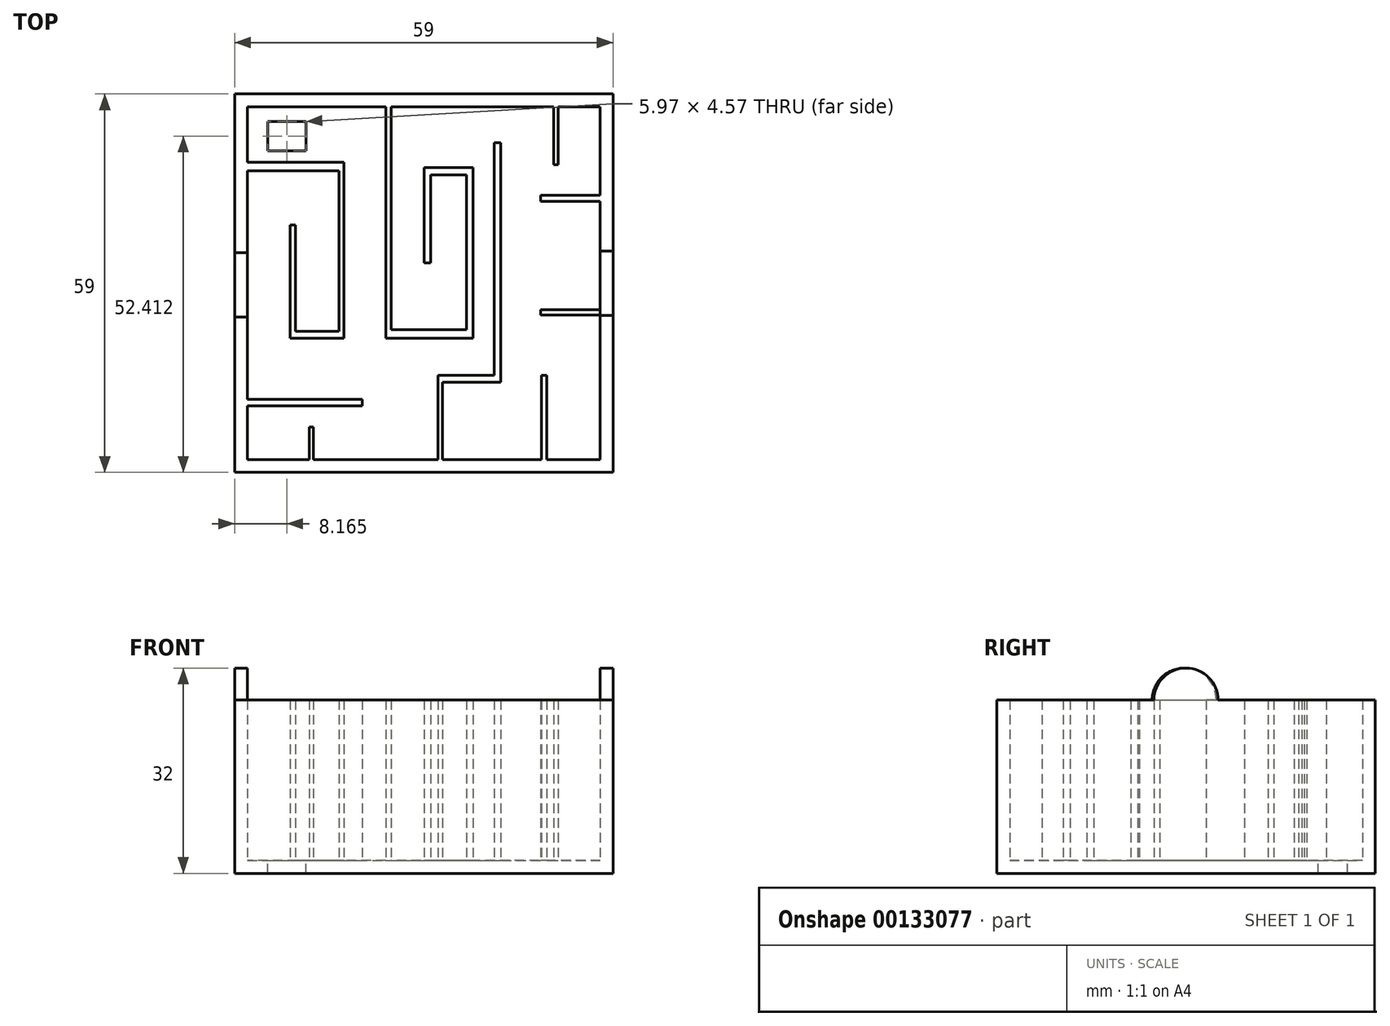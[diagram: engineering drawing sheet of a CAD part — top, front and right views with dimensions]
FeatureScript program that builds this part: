
annotation { "Feature Type Name" : "Feature", "Feature Type Description" : "" }
export const myFeature = defineFeature(function(context is Context, id is Id, definition is map)
    precondition{}
    {
        {
            var Q0;
            Q0=qCreatedBy(makeId("Top.planeOp"),FACE);
            var sketch = newSketch(context, id + "F0", { "sketchPlane" : qUnion([Q0])});
            skLineSegment(sketch, "E0.bottom", {"start": v(0, 0) * mm, "end": v(55, 0) * mm});
            skLineSegment(sketch, "E0.top", {"start": v(0, 55) * mm, "end": v(55, 55) * mm});
            skLineSegment(sketch, "E0.left", {"start": v(0, 0) * mm, "end": v(0, 55) * mm});
            skLineSegment(sketch, "E0.right", {"start": v(55, 0) * mm, "end": v(55, 55) * mm});
            skSolve(sketch);
        }
        {
            var Q0;
            Q0=makeQuery(id+"F0.imprint","IMPRINT",FACE,{"disambiguationData":[TD([[makeQuery(id+"F0.imprint","IMPRINT",EDGE,{"derivedFrom":sQuery(id+"F0.wireOp",EDGE,"E0.bottom")}),1.0]])]});
            extrude(context, id + "F1", {"entities" : qUnion([Q0]), "depth" : 2 * mm});
        }
        {
            var Q0;
            Q0=makeQuery(id+"F1.opExtrude","CAP_FACE",FACE,{"disambiguationData":[OSD([sQuery(id+"F0.wireOp",EDGE,"E0.bottom"),sQuery(id+"F0.wireOp",EDGE,"E0.top"),sQuery(id+"F0.wireOp",EDGE,"E0.left"),sQuery(id+"F0.wireOp",EDGE,"E0.right")])],"isStart":false});
            var sketch = newSketch(context, id + "F2", { "sketchPlane" : qUnion([Q0])});
            skLineSegment(sketch, "E1.bottom", {"start": v(46.66, 0) * mm, "end": v(45.82, 0) * mm});
            skLineSegment(sketch, "E1.top", {"start": v(46.66, 13.1) * mm, "end": v(45.82, 13.1) * mm});
            skLineSegment(sketch, "E1.left", {"start": v(46.66, 0) * mm, "end": v(46.66, 13.1) * mm});
            skLineSegment(sketch, "E1.right", {"start": v(45.82, 0) * mm, "end": v(45.82, 13.1) * mm});
            skLineSegment(sketch, "E2.bottom", {"start": v(0, 46.34) * mm, "end": v(14.3, 46.34) * mm});
            skLineSegment(sketch, "E2.top", {"start": v(0, 45.02) * mm, "end": v(14.3, 45.02) * mm});
            skLineSegment(sketch, "E2.left", {"start": v(0, 46.34) * mm, "end": v(0, 45.02) * mm});
            skLineSegment(sketch, "E2.right", {"start": v(14.3, 46.34) * mm, "end": v(14.3, 45.02) * mm});
            skLineSegment(sketch, "E3.bottom", {"start": v(14.3, 46.34) * mm, "end": v(15.04, 46.34) * mm});
            skLineSegment(sketch, "E3.top", {"start": v(14.3, 19.96) * mm, "end": v(15.04, 19.96) * mm});
            skLineSegment(sketch, "E3.left", {"start": v(14.3, 46.34) * mm, "end": v(14.3, 19.96) * mm});
            skLineSegment(sketch, "E3.right", {"start": v(15.04, 46.34) * mm, "end": v(15.04, 19.96) * mm});
            skLineSegment(sketch, "E4.bottom", {"start": v(15.04, 19.96) * mm, "end": v(7.49, 19.96) * mm});
            skLineSegment(sketch, "E4.top", {"start": v(15.04, 18.9) * mm, "end": v(7.49, 18.9) * mm});
            skLineSegment(sketch, "E4.left", {"start": v(15.04, 19.96) * mm, "end": v(15.04, 18.9) * mm});
            skLineSegment(sketch, "E4.right", {"start": v(7.49, 19.96) * mm, "end": v(7.49, 18.9) * mm});
            skLineSegment(sketch, "E5.bottom", {"start": v(7.49, 18.9) * mm, "end": v(6.65, 18.9) * mm});
            skLineSegment(sketch, "E5.top", {"start": v(7.49, 36.58) * mm, "end": v(6.65, 36.58) * mm});
            skLineSegment(sketch, "E5.left", {"start": v(7.49, 18.9) * mm, "end": v(7.49, 36.58) * mm});
            skLineSegment(sketch, "E5.right", {"start": v(6.65, 18.9) * mm, "end": v(6.65, 36.58) * mm});
            skLineSegment(sketch, "E6.bottom", {"start": v(0, 9.41) * mm, "end": v(17.94, 9.41) * mm});
            skLineSegment(sketch, "E6.top", {"start": v(0, 8.36) * mm, "end": v(17.94, 8.36) * mm});
            skLineSegment(sketch, "E6.left", {"start": v(0, 9.41) * mm, "end": v(0, 8.36) * mm});
            skLineSegment(sketch, "E6.right", {"start": v(17.94, 9.41) * mm, "end": v(17.94, 8.36) * mm});
            skLineSegment(sketch, "E7.bottom", {"start": v(10.29, 0) * mm, "end": v(9.63, 0) * mm});
            skLineSegment(sketch, "E7.top", {"start": v(10.29, 5.06) * mm, "end": v(9.63, 5.06) * mm});
            skLineSegment(sketch, "E7.left", {"start": v(10.29, 0) * mm, "end": v(10.29, 5.06) * mm});
            skLineSegment(sketch, "E7.right", {"start": v(9.63, 0) * mm, "end": v(9.63, 5.06) * mm});
            skLineSegment(sketch, "E8.bottom", {"start": v(21.57, 55) * mm, "end": v(22.41, 55) * mm});
            skLineSegment(sketch, "E8.top", {"start": v(21.57, 18.9) * mm, "end": v(22.41, 18.9) * mm});
            skLineSegment(sketch, "E8.left", {"start": v(21.57, 55) * mm, "end": v(21.57, 18.9) * mm});
            skLineSegment(sketch, "E8.right", {"start": v(22.41, 55) * mm, "end": v(22.41, 18.9) * mm});
            skLineSegment(sketch, "E9.bottom", {"start": v(22.41, 18.9) * mm, "end": v(35.19, 18.9) * mm});
            skLineSegment(sketch, "E9.top", {"start": v(22.41, 20.23) * mm, "end": v(35.19, 20.23) * mm});
            skLineSegment(sketch, "E9.left", {"start": v(22.41, 18.9) * mm, "end": v(22.41, 20.23) * mm});
            skLineSegment(sketch, "E9.right", {"start": v(35.19, 18.9) * mm, "end": v(35.19, 20.23) * mm});
            skLineSegment(sketch, "E10.bottom", {"start": v(35.19, 20.23) * mm, "end": v(34.16, 20.23) * mm});
            skLineSegment(sketch, "E10.top", {"start": v(35.19, 44.36) * mm, "end": v(34.16, 44.36) * mm});
            skLineSegment(sketch, "E10.left", {"start": v(35.19, 20.23) * mm, "end": v(35.19, 44.36) * mm});
            skLineSegment(sketch, "E10.right", {"start": v(34.16, 20.23) * mm, "end": v(34.16, 44.36) * mm});
            skLineSegment(sketch, "E11.bottom", {"start": v(35.19, 44.36) * mm, "end": v(28.57, 44.36) * mm});
            skLineSegment(sketch, "E11.top", {"start": v(35.19, 45.55) * mm, "end": v(28.57, 45.55) * mm});
            skLineSegment(sketch, "E11.left", {"start": v(35.19, 44.36) * mm, "end": v(35.19, 45.55) * mm});
            skLineSegment(sketch, "E11.right", {"start": v(28.57, 44.36) * mm, "end": v(28.57, 45.55) * mm});
            skLineSegment(sketch, "E12.bottom", {"start": v(28.57, 45.55) * mm, "end": v(27.54, 45.55) * mm});
            skLineSegment(sketch, "E12.top", {"start": v(28.57, 30.65) * mm, "end": v(27.54, 30.65) * mm});
            skLineSegment(sketch, "E12.left", {"start": v(28.57, 45.55) * mm, "end": v(28.57, 30.65) * mm});
            skLineSegment(sketch, "E12.right", {"start": v(27.54, 45.55) * mm, "end": v(27.54, 30.65) * mm});
            skLineSegment(sketch, "E13.left", {"start": v(55, 27.5) * mm, "end": v(55, 26.03) * mm});
            skLineSegment(sketch, "E14.bottom", {"start": v(29.69, 0) * mm, "end": v(30.43, 0) * mm});
            skLineSegment(sketch, "E14.top", {"start": v(29.69, 13.1) * mm, "end": v(30.43, 13.1) * mm});
            skLineSegment(sketch, "E14.left", {"start": v(29.69, 0) * mm, "end": v(29.69, 13.1) * mm});
            skLineSegment(sketch, "E14.right", {"start": v(30.43, 0) * mm, "end": v(30.43, 13.1) * mm});
            skLineSegment(sketch, "E15.bottom", {"start": v(29.69, 13.1) * mm, "end": v(38.45, 13.1) * mm});
            skLineSegment(sketch, "E15.top", {"start": v(29.69, 12.05) * mm, "end": v(38.45, 12.05) * mm});
            skLineSegment(sketch, "E15.left", {"start": v(29.69, 13.1) * mm, "end": v(29.69, 12.05) * mm});
            skLineSegment(sketch, "E15.right", {"start": v(38.45, 13.1) * mm, "end": v(38.45, 12.05) * mm});
            skLineSegment(sketch, "E16.bottom", {"start": v(38.45, 12.05) * mm, "end": v(39.48, 12.05) * mm});
            skLineSegment(sketch, "E16.top", {"start": v(38.45, 49.38) * mm, "end": v(39.48, 49.38) * mm});
            skLineSegment(sketch, "E16.left", {"start": v(38.45, 12.05) * mm, "end": v(38.45, 49.38) * mm});
            skLineSegment(sketch, "E16.right", {"start": v(39.48, 12.05) * mm, "end": v(39.48, 49.38) * mm});
            skLineSegment(sketch, "E17.bottom", {"start": v(55, 41.2) * mm, "end": v(45.73, 41.2) * mm});
            skLineSegment(sketch, "E17.top", {"start": v(55, 40.28) * mm, "end": v(45.73, 40.28) * mm});
            skLineSegment(sketch, "E17.left", {"start": v(55, 41.2) * mm, "end": v(55, 40.28) * mm});
            skLineSegment(sketch, "E17.right", {"start": v(45.73, 41.2) * mm, "end": v(45.73, 40.28) * mm});
            skLineSegment(sketch, "E18.bottom", {"start": v(47.78, 55) * mm, "end": v(48.43, 55) * mm});
            skLineSegment(sketch, "E18.top", {"start": v(47.78, 45.95) * mm, "end": v(48.43, 45.95) * mm});
            skLineSegment(sketch, "E18.left", {"start": v(47.78, 55) * mm, "end": v(47.78, 45.95) * mm});
            skLineSegment(sketch, "E18.right", {"start": v(48.43, 55) * mm, "end": v(48.43, 45.95) * mm});
            skLineSegment(sketch, "E19.bottom", {"start": v(55, 23.38) * mm, "end": v(45.7, 23.38) * mm});
            skLineSegment(sketch, "E19.top", {"start": v(55, 22.5) * mm, "end": v(45.7, 22.5) * mm});
            skLineSegment(sketch, "E19.left", {"start": v(55, 23.38) * mm, "end": v(55, 22.5) * mm});
            skLineSegment(sketch, "E19.right", {"start": v(45.7, 23.38) * mm, "end": v(45.7, 22.5) * mm});
            skSolve(sketch);
        }
        {
            var Q0;
            Q0 = qSketchRegion(id + "F2", true);
            extrude(context, id + "F3", {"entities" : qUnion([Q0]), "operationType" : NewBodyOperationType.ADD, "depth" : 25 * mm});
        }
        {
            var Q0;
            Q0=makeQuery(id+"F3.boolean.opBoolean","MERGE",FACE,{"derivedFrom":[makeQuery(id+"F1.opExtrude","SWEPT_FACE",FACE,{"disambiguationData":[OSD([sQuery(id+"F0.wireOp",EDGE,"E0.bottom")])]}),makeQuery(id+"F3.opExtrude","SWEPT_FACE",FACE,{"disambiguationData":[OSD([sQuery(id+"F2.wireOp",EDGE,"E1.bottom")])]}),makeQuery(id+"F3.opExtrude","SWEPT_FACE",FACE,{"disambiguationData":[OSD([sQuery(id+"F2.wireOp",EDGE,"E7.bottom")])]}),makeQuery(id+"F3.opExtrude","SWEPT_FACE",FACE,{"disambiguationData":[OSD([sQuery(id+"F2.wireOp",EDGE,"E14.bottom")])]})]});
            var sketch = newSketch(context, id + "F4", { "sketchPlane" : qUnion([Q0])});
            skLineSegment(sketch, "E20.bottom", {"start": v(0, 2) * mm, "end": v(55, 2) * mm});
            skLineSegment(sketch, "E20.top", {"start": v(0, 0) * mm, "end": v(55, 0) * mm});
            skLineSegment(sketch, "E20.left", {"start": v(0, 2) * mm, "end": v(0, 0) * mm});
            skLineSegment(sketch, "E20.right", {"start": v(55, 2) * mm, "end": v(55, 0) * mm});
            skSolve(sketch);
        }
        {
            var Q0;
            Q0=makeQuery(id+"F4.imprint","IMPRINT",FACE,{"disambiguationData":[TD([[makeQuery(id+"F4.imprint","IMPRINT",EDGE,{"derivedFrom":sQuery(id+"F4.wireOp",EDGE,"E20.top")}),1.0]])]});
            extrude(context, id + "F5", {"entities" : qUnion([Q0]), "operationType" : NewBodyOperationType.ADD, "depth" : 2 * mm});
        }
        {
            var Q0;
            Q0=makeQuery(id+"F5.boolean.opBoolean","MERGE",FACE,{"derivedFrom":[makeQuery(id+"F1.opExtrude","CAP_FACE",FACE,{"disambiguationData":[OSD([sQuery(id+"F0.wireOp",EDGE,"E0.bottom"),sQuery(id+"F0.wireOp",EDGE,"E0.top"),sQuery(id+"F0.wireOp",EDGE,"E0.left"),sQuery(id+"F0.wireOp",EDGE,"E0.right")])],"isStart":false}),makeQuery(id+"F5.opExtrude","SWEPT_FACE",FACE,{"disambiguationData":[OSD([sQuery(id+"F4.wireOp",EDGE,"E20.bottom")])]})]});
            var sketch = newSketch(context, id + "F6", { "sketchPlane" : qUnion([Q0])});
            skLineSegment(sketch, "E21.bottom", {"start": v(0, 0) * mm, "end": v(55, 0) * mm});
            skLineSegment(sketch, "E21.top", {"start": v(0, -2) * mm, "end": v(55, -2) * mm});
            skLineSegment(sketch, "E21.left", {"start": v(0, 0) * mm, "end": v(0, -2) * mm});
            skLineSegment(sketch, "E21.right", {"start": v(55, 0) * mm, "end": v(55, -2) * mm});
            skSolve(sketch);
        }
        {
            var Q0;
            Q0=makeQuery(id+"F6.imprint","IMPRINT",FACE,{"disambiguationData":[TD([[makeQuery(id+"F6.imprint","IMPRINT",EDGE,{"derivedFrom":sQuery(id+"F6.wireOp",EDGE,"E21.top")}),1.0]])]});
            extrude(context, id + "F7", {"entities" : qUnion([Q0]), "operationType" : NewBodyOperationType.ADD, "depth" : 25 * mm});
        }
        {
            var Q0;
            Q0=makeQuery(id+"F7.boolean.opBoolean","MERGE",FACE,{"derivedFrom":[makeQuery(id+"F5.boolean.opBoolean","MERGE",FACE,{"derivedFrom":[makeQuery(id+"F3.boolean.opBoolean","MERGE",FACE,{"derivedFrom":[makeQuery(id+"F1.opExtrude","SWEPT_FACE",FACE,{"disambiguationData":[OSD([sQuery(id+"F0.wireOp",EDGE,"E0.left")])]}),makeQuery(id+"F3.opExtrude","SWEPT_FACE",FACE,{"disambiguationData":[OSD([sQuery(id+"F2.wireOp",EDGE,"E2.left")])]}),makeQuery(id+"F3.opExtrude","SWEPT_FACE",FACE,{"disambiguationData":[OSD([sQuery(id+"F2.wireOp",EDGE,"E6.left")])]})]}),makeQuery(id+"F5.opExtrude","SWEPT_FACE",FACE,{"disambiguationData":[OSD([sQuery(id+"F4.wireOp",EDGE,"E20.left")])]})]}),makeQuery(id+"F7.opExtrude","SWEPT_FACE",FACE,{"disambiguationData":[OSD([sQuery(id+"F6.wireOp",EDGE,"E21.left")])]})]});
            var sketch = newSketch(context, id + "F8", { "sketchPlane" : qUnion([Q0])});
            skLineSegment(sketch, "E22.bottom", {"start": v(-55, 2) * mm, "end": v(2, 2) * mm});
            skLineSegment(sketch, "E22.top", {"start": v(-55, 0) * mm, "end": v(2, 0) * mm});
            skLineSegment(sketch, "E22.left", {"start": v(-55, 2) * mm, "end": v(-55, 0) * mm});
            skLineSegment(sketch, "E22.right", {"start": v(2, 2) * mm, "end": v(2, 0) * mm});
            skSolve(sketch);
        }
        {
            var Q0;
            Q0 = qSketchRegion(id + "F8", true);
            extrude(context, id + "F9", {"entities" : qUnion([Q0]), "operationType" : NewBodyOperationType.ADD, "depth" : 2 * mm});
        }
        {
            var Q0;
            Q0=makeQuery(id+"F9.boolean.opBoolean","MERGE",FACE,{"derivedFrom":[makeQuery(id+"F5.boolean.opBoolean","MERGE",FACE,{"derivedFrom":[makeQuery(id+"F1.opExtrude","CAP_FACE",FACE,{"disambiguationData":[OSD([sQuery(id+"F0.wireOp",EDGE,"E0.bottom"),sQuery(id+"F0.wireOp",EDGE,"E0.top"),sQuery(id+"F0.wireOp",EDGE,"E0.left"),sQuery(id+"F0.wireOp",EDGE,"E0.right")])],"isStart":false}),makeQuery(id+"F5.opExtrude","SWEPT_FACE",FACE,{"disambiguationData":[OSD([sQuery(id+"F4.wireOp",EDGE,"E20.bottom")])]})]}),makeQuery(id+"F9.opExtrude","SWEPT_FACE",FACE,{"disambiguationData":[OSD([sQuery(id+"F8.wireOp",EDGE,"E22.bottom")])]})]});
            var sketch = newSketch(context, id + "F10", { "sketchPlane" : qUnion([Q0])});
            skLineSegment(sketch, "E23.bottom", {"start": v(0, 55) * mm, "end": v(-2, 55) * mm});
            skLineSegment(sketch, "E23.top", {"start": v(0, -2) * mm, "end": v(-2, -2) * mm});
            skLineSegment(sketch, "E23.left", {"start": v(0, 55) * mm, "end": v(0, -2) * mm});
            skLineSegment(sketch, "E23.right", {"start": v(-2, 55) * mm, "end": v(-2, -2) * mm});
            skSolve(sketch);
        }
        {
            var Q0;
            Q0 = qSketchRegion(id + "F10", true);
            extrude(context, id + "F11", {"entities" : qUnion([Q0]), "operationType" : NewBodyOperationType.ADD, "depth" : 25 * mm});
        }
        {
            var Q0;
            Q0=makeQuery(id+"F11.boolean.opBoolean","MERGE",FACE,{"derivedFrom":[makeQuery(id+"F9.boolean.opBoolean","MERGE",FACE,{"derivedFrom":[makeQuery(id+"F3.boolean.opBoolean","MERGE",FACE,{"derivedFrom":[makeQuery(id+"F1.opExtrude","SWEPT_FACE",FACE,{"disambiguationData":[OSD([sQuery(id+"F0.wireOp",EDGE,"E0.top")])]}),makeQuery(id+"F3.opExtrude","SWEPT_FACE",FACE,{"disambiguationData":[OSD([sQuery(id+"F2.wireOp",EDGE,"E8.bottom")])]}),makeQuery(id+"F3.opExtrude","SWEPT_FACE",FACE,{"disambiguationData":[OSD([sQuery(id+"F2.wireOp",EDGE,"E18.bottom")])]})]}),makeQuery(id+"F9.opExtrude","SWEPT_FACE",FACE,{"disambiguationData":[OSD([sQuery(id+"F8.wireOp",EDGE,"E22.left")])]})]}),makeQuery(id+"F11.opExtrude","SWEPT_FACE",FACE,{"disambiguationData":[OSD([sQuery(id+"F10.wireOp",EDGE,"E23.bottom")])]})]});
            var sketch = newSketch(context, id + "F12", { "sketchPlane" : qUnion([Q0])});
            skLineSegment(sketch, "E24.bottom", {"start": v(2, 0) * mm, "end": v(-55, 0) * mm});
            skLineSegment(sketch, "E24.top", {"start": v(2, 2) * mm, "end": v(-55, 2) * mm});
            skLineSegment(sketch, "E24.left", {"start": v(2, 0) * mm, "end": v(2, 2) * mm});
            skLineSegment(sketch, "E24.right", {"start": v(-55, 0) * mm, "end": v(-55, 2) * mm});
            skSolve(sketch);
        }
        {
            var Q0;
            Q0=makeQuery(id+"F12.imprint","IMPRINT",FACE,{"disambiguationData":[TD([[makeQuery(id+"F12.imprint","IMPRINT",EDGE,{"derivedFrom":sQuery(id+"F12.wireOp",EDGE,"E24.bottom")}),-1.0]])]});
            extrude(context, id + "F13", {"entities" : qUnion([Q0]), "operationType" : NewBodyOperationType.ADD, "depth" : 2 * mm});
        }
        {
            var Q0;
            Q0=makeQuery(id+"F13.boolean.opBoolean","MERGE",FACE,{"derivedFrom":[makeQuery(id+"F9.boolean.opBoolean","MERGE",FACE,{"derivedFrom":[makeQuery(id+"F5.boolean.opBoolean","MERGE",FACE,{"derivedFrom":[makeQuery(id+"F1.opExtrude","CAP_FACE",FACE,{"disambiguationData":[OSD([sQuery(id+"F0.wireOp",EDGE,"E0.bottom"),sQuery(id+"F0.wireOp",EDGE,"E0.top"),sQuery(id+"F0.wireOp",EDGE,"E0.left"),sQuery(id+"F0.wireOp",EDGE,"E0.right")])],"isStart":false}),makeQuery(id+"F5.opExtrude","SWEPT_FACE",FACE,{"disambiguationData":[OSD([sQuery(id+"F4.wireOp",EDGE,"E20.bottom")])]})]}),makeQuery(id+"F9.opExtrude","SWEPT_FACE",FACE,{"disambiguationData":[OSD([sQuery(id+"F8.wireOp",EDGE,"E22.bottom")])]})]}),makeQuery(id+"F13.opExtrude","SWEPT_FACE",FACE,{"disambiguationData":[OSD([sQuery(id+"F12.wireOp",EDGE,"E24.top")])]})]});
            var sketch = newSketch(context, id + "F14", { "sketchPlane" : qUnion([Q0])});
            skLineSegment(sketch, "E25.bottom", {"start": v(55, 57) * mm, "end": v(-2, 57) * mm});
            skLineSegment(sketch, "E25.top", {"start": v(55, 55) * mm, "end": v(-2, 55) * mm});
            skLineSegment(sketch, "E25.left", {"start": v(55, 57) * mm, "end": v(55, 55) * mm});
            skLineSegment(sketch, "E25.right", {"start": v(-2, 57) * mm, "end": v(-2, 55) * mm});
            skSolve(sketch);
        }
        {
            var Q0;
            Q0=makeQuery(id+"F14.imprint","IMPRINT",FACE,{"disambiguationData":[TD([[makeQuery(id+"F14.imprint","IMPRINT",EDGE,{"derivedFrom":sQuery(id+"F14.wireOp",EDGE,"E25.bottom")}),-1.0]])]});
            extrude(context, id + "F15", {"entities" : qUnion([Q0]), "operationType" : NewBodyOperationType.ADD, "depth" : 25 * mm});
        }
        {
            var Q0;
            Q0=makeQuery(id+"F15.boolean.opBoolean","MERGE",FACE,{"derivedFrom":[makeQuery(id+"F13.boolean.opBoolean","MERGE",FACE,{"derivedFrom":[makeQuery(id+"F7.boolean.opBoolean","MERGE",FACE,{"derivedFrom":[makeQuery(id+"F5.boolean.opBoolean","MERGE",FACE,{"derivedFrom":[makeQuery(id+"F3.boolean.opBoolean","MERGE",FACE,{"derivedFrom":[makeQuery(id+"F1.opExtrude","SWEPT_FACE",FACE,{"disambiguationData":[OSD([sQuery(id+"F0.wireOp",EDGE,"E0.right")])]}),makeQuery(id+"F3.opExtrude","SWEPT_FACE",FACE,{"disambiguationData":[OSD([sQuery(id+"F2.wireOp",EDGE,"E17.left")])]}),makeQuery(id+"F3.opExtrude","SWEPT_FACE",FACE,{"disambiguationData":[OSD([sQuery(id+"F2.wireOp",EDGE,"E19.left")])]})]}),makeQuery(id+"F5.opExtrude","SWEPT_FACE",FACE,{"disambiguationData":[OSD([sQuery(id+"F4.wireOp",EDGE,"E20.right")])]})]}),makeQuery(id+"F7.opExtrude","SWEPT_FACE",FACE,{"disambiguationData":[OSD([sQuery(id+"F6.wireOp",EDGE,"E21.right")])]})]}),makeQuery(id+"F13.opExtrude","SWEPT_FACE",FACE,{"disambiguationData":[OSD([sQuery(id+"F12.wireOp",EDGE,"E24.right")])]})]}),makeQuery(id+"F15.opExtrude","SWEPT_FACE",FACE,{"disambiguationData":[OSD([sQuery(id+"F14.wireOp",EDGE,"E25.left")])]})]});
            var sketch = newSketch(context, id + "F16", { "sketchPlane" : qUnion([Q0])});
            skLineSegment(sketch, "E26.bottom", {"start": v(-2, 0) * mm, "end": v(57, 0) * mm});
            skLineSegment(sketch, "E26.top", {"start": v(-2, 2) * mm, "end": v(57, 2) * mm});
            skLineSegment(sketch, "E26.left", {"start": v(-2, 0) * mm, "end": v(-2, 2) * mm});
            skLineSegment(sketch, "E26.right", {"start": v(57, 0) * mm, "end": v(57, 2) * mm});
            skSolve(sketch);
        }
        {
            var Q0;
            Q0=makeQuery(id+"F16.imprint","IMPRINT",FACE,{"disambiguationData":[TD([[makeQuery(id+"F16.imprint","IMPRINT",EDGE,{"derivedFrom":sQuery(id+"F16.wireOp",EDGE,"E26.bottom")}),1.0]])]});
            extrude(context, id + "F17", {"entities" : qUnion([Q0]), "operationType" : NewBodyOperationType.ADD, "depth" : 2 * mm});
        }
        {
            var Q0;
            Q0=makeQuery(id+"F17.boolean.opBoolean","MERGE",FACE,{"derivedFrom":[makeQuery(id+"F13.boolean.opBoolean","MERGE",FACE,{"derivedFrom":[makeQuery(id+"F9.boolean.opBoolean","MERGE",FACE,{"derivedFrom":[makeQuery(id+"F5.boolean.opBoolean","MERGE",FACE,{"derivedFrom":[makeQuery(id+"F1.opExtrude","CAP_FACE",FACE,{"disambiguationData":[OSD([sQuery(id+"F0.wireOp",EDGE,"E0.bottom"),sQuery(id+"F0.wireOp",EDGE,"E0.top"),sQuery(id+"F0.wireOp",EDGE,"E0.left"),sQuery(id+"F0.wireOp",EDGE,"E0.right")])],"isStart":false}),makeQuery(id+"F5.opExtrude","SWEPT_FACE",FACE,{"disambiguationData":[OSD([sQuery(id+"F4.wireOp",EDGE,"E20.bottom")])]})]}),makeQuery(id+"F9.opExtrude","SWEPT_FACE",FACE,{"disambiguationData":[OSD([sQuery(id+"F8.wireOp",EDGE,"E22.bottom")])]})]}),makeQuery(id+"F13.opExtrude","SWEPT_FACE",FACE,{"disambiguationData":[OSD([sQuery(id+"F12.wireOp",EDGE,"E24.top")])]})]}),makeQuery(id+"F17.opExtrude","SWEPT_FACE",FACE,{"disambiguationData":[OSD([sQuery(id+"F16.wireOp",EDGE,"E26.top")])]})]});
            var sketch = newSketch(context, id + "F18", { "sketchPlane" : qUnion([Q0])});
            skLineSegment(sketch, "E27.bottom", {"start": v(57, 57) * mm, "end": v(55, 57) * mm});
            skLineSegment(sketch, "E27.top", {"start": v(57, -2) * mm, "end": v(55, -2) * mm});
            skLineSegment(sketch, "E27.left", {"start": v(57, 57) * mm, "end": v(57, -2) * mm});
            skLineSegment(sketch, "E27.right", {"start": v(55, 57) * mm, "end": v(55, -2) * mm});
            skSolve(sketch);
        }
        {
            var Q0;
            {var subQ12=sQuery(id+"F18.wireOp",EDGE,"E27.bottom");Q0=makeQuery(id+"F18.imprint","IMPRINT",FACE,{"disambiguationData":[TD([[makeQuery(id+"F18.imprint","IMPRINT",EDGE,{"derivedFrom":subQ12}),1.0]])]});}
            extrude(context, id + "F19", {"entities" : qUnion([Q0]), "operationType" : NewBodyOperationType.ADD, "depth" : 25 * mm});
        }
        {
            var Q0;
            Q0=makeQuery(id+"F17.boolean.opBoolean","MERGE",FACE,{"derivedFrom":[makeQuery(id+"F13.boolean.opBoolean","MERGE",FACE,{"derivedFrom":[makeQuery(id+"F9.boolean.opBoolean","MERGE",FACE,{"derivedFrom":[makeQuery(id+"F5.boolean.opBoolean","MERGE",FACE,{"derivedFrom":[makeQuery(id+"F1.opExtrude","CAP_FACE",FACE,{"disambiguationData":[OSD([sQuery(id+"F0.wireOp",EDGE,"E0.bottom"),sQuery(id+"F0.wireOp",EDGE,"E0.top"),sQuery(id+"F0.wireOp",EDGE,"E0.left"),sQuery(id+"F0.wireOp",EDGE,"E0.right")])],"isStart":false}),makeQuery(id+"F5.opExtrude","SWEPT_FACE",FACE,{"disambiguationData":[OSD([sQuery(id+"F4.wireOp",EDGE,"E20.bottom")])]})]}),makeQuery(id+"F9.opExtrude","SWEPT_FACE",FACE,{"disambiguationData":[OSD([sQuery(id+"F8.wireOp",EDGE,"E22.bottom")])]})]}),makeQuery(id+"F13.opExtrude","SWEPT_FACE",FACE,{"disambiguationData":[OSD([sQuery(id+"F12.wireOp",EDGE,"E24.top")])]})]}),makeQuery(id+"F17.opExtrude","SWEPT_FACE",FACE,{"disambiguationData":[OSD([sQuery(id+"F16.wireOp",EDGE,"E26.top")])]})]});
            var sketch = newSketch(context, id + "F20", { "sketchPlane" : qUnion([Q0])});
            skLineSegment(sketch, "E28.bottom", {"start": v(3.18, 52.7) * mm, "end": v(9.15, 52.7) * mm});
            skLineSegment(sketch, "E28.top", {"start": v(3.18, 48.13) * mm, "end": v(9.15, 48.13) * mm});
            skLineSegment(sketch, "E28.left", {"start": v(3.18, 52.7) * mm, "end": v(3.18, 48.13) * mm});
            skLineSegment(sketch, "E28.right", {"start": v(9.15, 52.7) * mm, "end": v(9.15, 48.13) * mm});
            skSolve(sketch);
        }
        {
            var Q0;
            Q0 = qSketchRegion(id + "F20", true);
            var Q1;
            Q1=makeQuery(id+"F20.imprint","IMPRINT",FACE,{"disambiguationData":[TD([[makeQuery(id+"F20.imprint","IMPRINT",EDGE,{"derivedFrom":sQuery(id+"F20.wireOp",EDGE,"E28.bottom")}),-1.0]])]});
            extrude(context, id + "F21", {"entities" : qUnion([Q0, Q1]), "operationType" : NewBodyOperationType.REMOVE, "oppositeDirection" : true, "depth" : 25 * mm});
        }
        {
            var Q0;
            Q0=makeQuery(id+"F19.boolean.opBoolean","MERGE",FACE,{"derivedFrom":[makeQuery(id+"F17.boolean.opBoolean","MERGE",FACE,{"derivedFrom":[makeQuery(id+"F15.boolean.opBoolean","MERGE",FACE,{"derivedFrom":[makeQuery(id+"F13.opExtrude","CAP_FACE",FACE,{"disambiguationData":[OSD([sQuery(id+"F12.wireOp",EDGE,"E24.bottom"),sQuery(id+"F12.wireOp",EDGE,"E24.top"),sQuery(id+"F12.wireOp",EDGE,"E24.left"),sQuery(id+"F12.wireOp",EDGE,"E24.right")])],"isStart":false}),makeQuery(id+"F15.opExtrude","SWEPT_FACE",FACE,{"disambiguationData":[OSD([sQuery(id+"F14.wireOp",EDGE,"E25.bottom")])]})]}),makeQuery(id+"F17.opExtrude","SWEPT_FACE",FACE,{"disambiguationData":[OSD([sQuery(id+"F16.wireOp",EDGE,"E26.right")])]})]}),makeQuery(id+"F19.opExtrude","SWEPT_FACE",FACE,{"disambiguationData":[OSD([sQuery(id+"F18.wireOp",EDGE,"E27.bottom")])]})]});
            var sketch = newSketch(context, id + "F22", { "sketchPlane" : qUnion([Q0])});
            skSolve(sketch);
        }
        {
            var Q0;
            Q0=makeQuery(id+"F19.boolean.opBoolean","MERGE",FACE,{"derivedFrom":[makeQuery(id+"F17.opExtrude","CAP_FACE",FACE,{"disambiguationData":[OSD([sQuery(id+"F16.wireOp",EDGE,"E26.bottom"),sQuery(id+"F16.wireOp",EDGE,"E26.top"),sQuery(id+"F16.wireOp",EDGE,"E26.left"),sQuery(id+"F16.wireOp",EDGE,"E26.right")])],"isStart":false}),makeQuery(id+"F19.opExtrude","SWEPT_FACE",FACE,{"disambiguationData":[OSD([sQuery(id+"F18.wireOp",EDGE,"E27.left")])]})]});
            var sketch = newSketch(context, id + "F23", { "sketchPlane" : qUnion([Q0])});
            skLineSegment(sketch, "E29.0", {"start": v(-2, 27) * mm, "end": v(57, 27) * mm});
            skCircle(sketch, "E30", {"center": v(27.5, 27) * mm, "radius": 5 * mm});
            skSolve(sketch);
        }
        {
            var Q0;
            {var subQ0=sQuery(id+"F23.wireOp",EDGE,"E30");var subQ1=sQuery(id+"F23.wireOp",EDGE,"E29.0");var subQ2=makeQuery(id+"F23.imprint","INTERSECT",VERTEX,{"disambiguationData":[OD(0.0)],"derivedFrom":[subQ1,subQ0]});Q0=makeQuery(id+"F23.imprint","IMPRINT",FACE,{"disambiguationData":[TD([[makeQuery(id+"F23.imprint","IMPRINT",EDGE,{"disambiguationData":[TD([[subQ2,-1.0]])],"derivedFrom":subQ1}),1.0]])]});}
            var Q1;
            {var subQ0=sQuery(id+"F2.wireOp",EDGE,"E17.top");var subQ1=sQuery(id+"F18.wireOp",EDGE,"E27.right");Q1=makeQuery(id+"F19.boolean.opBoolean","SPLIT",FACE,{"disambiguationData":[TD([makeQuery(id+"F3.opExtrude","SWEPT_FACE",FACE,{"disambiguationData":[OSD([subQ0])]})])],"derivedFrom":makeQuery(id+"F19.opExtrude","SWEPT_FACE",FACE,{"disambiguationData":[OSD([subQ1])]})});}
            extrude(context, id + "F24", {"entities" : qUnion([Q0]), "operationType" : NewBodyOperationType.ADD, "endBound" : BoundingType.UP_TO_SURFACE, "oppositeDirection" : true, "endBoundEntityFace" : qUnion([Q1]), "depth" : 25 * mm});
        }
        {
            var Q0;
            {var subQ1=sQuery(id+"F2.wireOp",EDGE,"E2.top");var subQ2=sQuery(id+"F10.wireOp",EDGE,"E23.left");Q0=makeQuery(id+"F11.boolean.opBoolean","SPLIT",FACE,{"disambiguationData":[TD([makeQuery(id+"F3.opExtrude","SWEPT_FACE",FACE,{"disambiguationData":[OSD([subQ1])]})])],"derivedFrom":makeQuery(id+"F11.opExtrude","SWEPT_FACE",FACE,{"disambiguationData":[OSD([subQ2])]})});}
            var sketch = newSketch(context, id + "F25", { "sketchPlane" : qUnion([Q0])});
            skLineSegment(sketch, "E31.0", {"start": v(45.02, 27) * mm, "end": v(9.41, 27) * mm});
            skCircle(sketch, "E32", {"center": v(27.22, 27) * mm, "radius": 5 * mm});
            skSolve(sketch);
        }
        {
            var Q0;
            {var subQ0=sQuery(id+"F25.wireOp",EDGE,"E32");var subQ1=sQuery(id+"F25.wireOp",EDGE,"E31.0");var subQ2=makeQuery(id+"F25.imprint","INTERSECT",VERTEX,{"disambiguationData":[OD(0.0)],"derivedFrom":[subQ1,subQ0]});Q0=makeQuery(id+"F25.imprint","IMPRINT",FACE,{"disambiguationData":[TD([[makeQuery(id+"F25.imprint","IMPRINT",EDGE,{"disambiguationData":[TD([[subQ2,-1.0]])],"derivedFrom":subQ1}),-1.0]])]});}
            var Q1;
            Q1=makeQuery(id+"F15.boolean.opBoolean","MERGE",FACE,{"derivedFrom":[makeQuery(id+"F13.boolean.opBoolean","MERGE",FACE,{"derivedFrom":[makeQuery(id+"F11.boolean.opBoolean","MERGE",FACE,{"derivedFrom":[makeQuery(id+"F9.opExtrude","CAP_FACE",FACE,{"disambiguationData":[OSD([sQuery(id+"F8.wireOp",EDGE,"E22.bottom"),sQuery(id+"F8.wireOp",EDGE,"E22.top"),sQuery(id+"F8.wireOp",EDGE,"E22.left"),sQuery(id+"F8.wireOp",EDGE,"E22.right")])],"isStart":false}),makeQuery(id+"F11.opExtrude","SWEPT_FACE",FACE,{"disambiguationData":[OSD([sQuery(id+"F10.wireOp",EDGE,"E23.right")])]})]}),makeQuery(id+"F13.opExtrude","SWEPT_FACE",FACE,{"disambiguationData":[OSD([sQuery(id+"F12.wireOp",EDGE,"E24.left")])]})]}),makeQuery(id+"F15.opExtrude","SWEPT_FACE",FACE,{"disambiguationData":[OSD([sQuery(id+"F14.wireOp",EDGE,"E25.right")])]})]});
            extrude(context, id + "F26", {"entities" : qUnion([Q0]), "operationType" : NewBodyOperationType.ADD, "endBound" : BoundingType.UP_TO_SURFACE, "oppositeDirection" : true, "endBoundEntityFace" : qUnion([Q1]), "depth" : 25 * mm});
        }
    });
